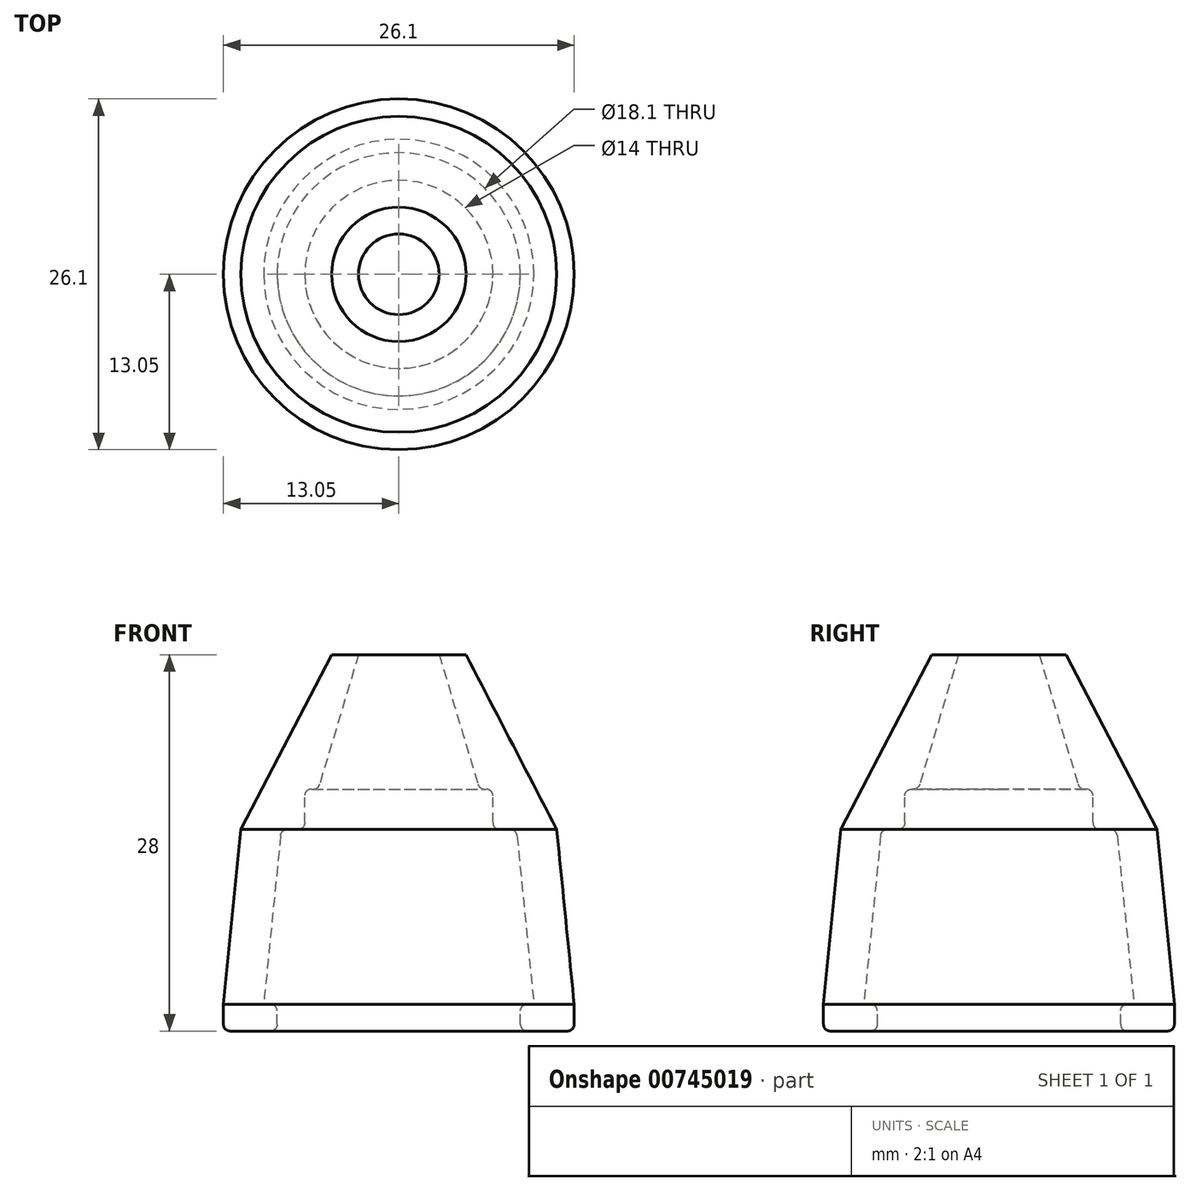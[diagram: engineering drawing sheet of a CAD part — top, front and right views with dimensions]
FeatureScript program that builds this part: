
annotation { "Feature Type Name" : "Feature", "Feature Type Description" : "" }
export const myFeature = defineFeature(function(context is Context, id is Id, definition is map)
    precondition{}
    {
        {
            var Q0;
            Q0=qCreatedBy(makeId("Front.planeOp"),FACE);
            var sketch = newSketch(context, id + "F0", { "sketchPlane" : qUnion([Q0])});
            skLineSegment(sketch, "E0", {"start": v(7, 13) * mm, "end": v(8.75, 13) * mm});
            skLineSegment(sketch, "E1", {"start": v(8.75, 13) * mm, "end": v(10.05, 0) * mm});
            skLineSegment(sketch, "E2", {"start": v(11.75, 13) * mm, "end": v(13.05, 0) * mm});
            skLineSegment(sketch, "E3", {"start": v(7, 16) * mm, "end": v(7, 13) * mm});
            skLineSegment(sketch, "E4", {"start": v(3, 26) * mm, "end": v(5, 26) * mm});
            skLineSegment(sketch, "E5", {"start": v(5, 26) * mm, "end": v(11.75, 13) * mm});
            skLineSegment(sketch, "E6", {"start": v(10.05, 0) * mm, "end": v(9.05, 0) * mm});
            skLineSegment(sketch, "E7", {"start": v(9.05, 0) * mm, "end": v(9.05, -2) * mm});
            skLineSegment(sketch, "E8", {"start": v(9.05, -2) * mm, "end": v(13.05, -2) * mm});
            skLineSegment(sketch, "E9", {"start": v(13.05, -2) * mm, "end": v(13.05, 0) * mm});
            skLineSegment(sketch, "E10", {"start": v(7, 16) * mm, "end": v(6, 16) * mm});
            skLineSegment(sketch, "E11", {"start": v(6, 16) * mm, "end": v(3, 26) * mm});
            skLineSegment(sketch, "E12", {"start": v(0, 35.45) * mm, "end": v(0, -14.37) * mm, "construction": true});
            skSolve(sketch);
        }
        {
            var Q0;
            Q0=makeQuery(id+"F0.imprint","IMPRINT",FACE,{"disambiguationData":[TD([[makeQuery(id+"F0.imprint","IMPRINT",EDGE,{"derivedFrom":sQuery(id+"F0.wireOp",EDGE,"E0")}),1.0]])]});
            var Q1;
            Q1=sQuery(id+"F0.wireOp",EDGE,"E12");
            revolve(context, id + "F1", {"surfaceOperationType" : NewSurfaceOperationType.NEW, "entities" : qUnion([Q0]), "axis" : qUnion([Q1]), "revolveType" : RevolveType.FULL});
        }
        {
            var Q0;
            Q0=makeQuery(id+"F1.opRevolve","SWEPT_EDGE",EDGE,{"disambiguationData":[OSD([sQuery(id+"F0.wireOp",EDGE,"E8"),sQuery(id+"F0.wireOp",EDGE,"E9")])]});
            var Q1;
            Q1=makeQuery(id+"F1.opRevolve","SWEPT_EDGE",EDGE,{"disambiguationData":[OSD([sQuery(id+"F0.wireOp",EDGE,"E7"),sQuery(id+"F0.wireOp",EDGE,"E8")])]});
            var Q2;
            Q2=makeQuery(id+"F1.opRevolve","SWEPT_EDGE",EDGE,{"disambiguationData":[OSD([sQuery(id+"F0.wireOp",EDGE,"E6"),sQuery(id+"F0.wireOp",EDGE,"E7")])]});
            var Q3;
            Q3=makeQuery(id+"F1.opRevolve","SWEPT_EDGE",EDGE,{"disambiguationData":[OSD([sQuery(id+"F0.wireOp",EDGE,"E0"),sQuery(id+"F0.wireOp",EDGE,"E1")])]});
            var Q4;
            Q4=makeQuery(id+"F1.opRevolve","SWEPT_EDGE",EDGE,{"disambiguationData":[OSD([sQuery(id+"F0.wireOp",EDGE,"E0"),sQuery(id+"F0.wireOp",EDGE,"E3")])]});
            var Q5;
            Q5=makeQuery(id+"F1.opRevolve","SWEPT_EDGE",EDGE,{"disambiguationData":[OSD([sQuery(id+"F0.wireOp",EDGE,"E3"),sQuery(id+"F0.wireOp",EDGE,"E10")])]});
            var Q6;
            Q6=makeQuery(id+"F1.opRevolve","SWEPT_EDGE",EDGE,{"disambiguationData":[OSD([sQuery(id+"F0.wireOp",EDGE,"E10"),sQuery(id+"F0.wireOp",EDGE,"E11")])]});
            fillet(context, id + "F2", {"entities" : qUnion([Q0, Q1, Q2, Q3, Q4, Q5, Q6]), "tangentPropagation" : true, "radius" : 0.5 * mm, "defaultsChanged" : false, "vertexSettings" : [], "allowEdgeOverflow" : false});
        }
    });
